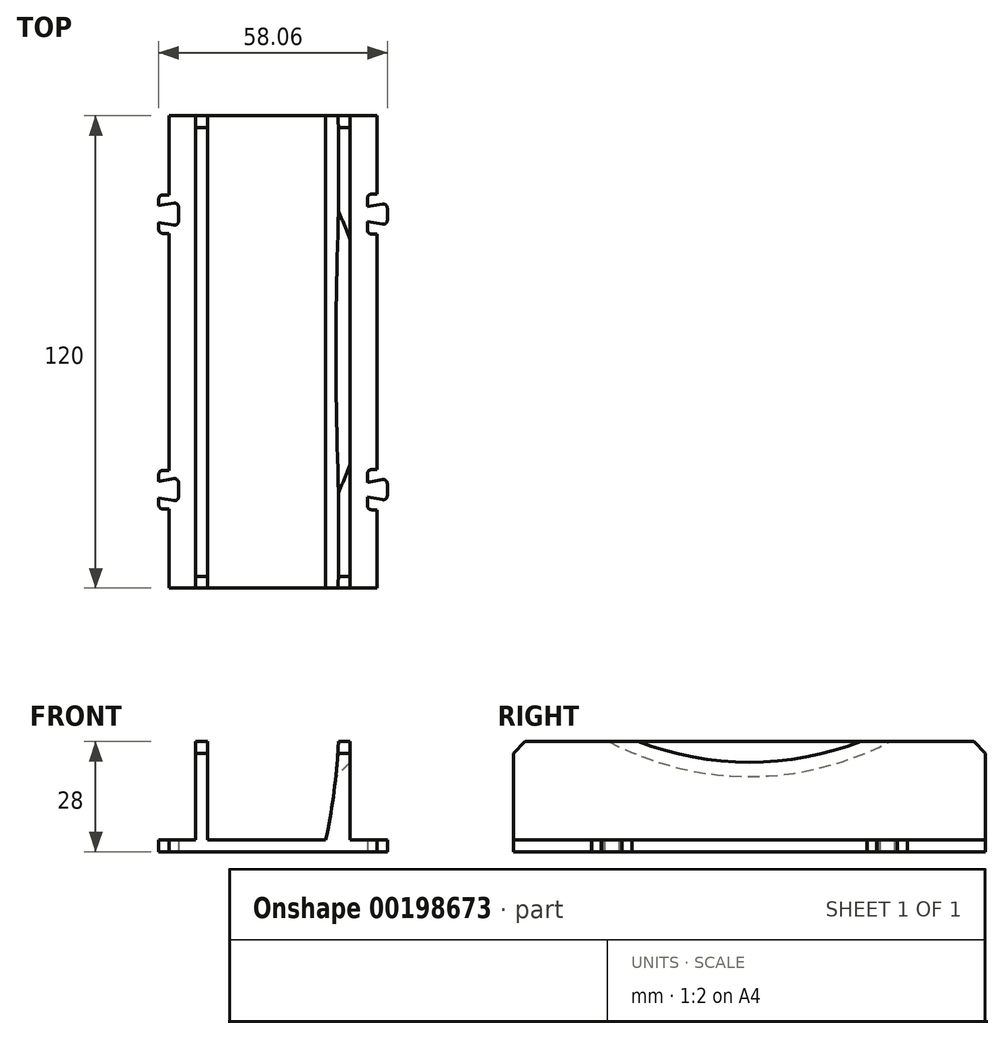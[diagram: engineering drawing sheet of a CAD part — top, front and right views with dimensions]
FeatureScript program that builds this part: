
annotation { "Feature Type Name" : "Feature", "Feature Type Description" : "" }
export const myFeature = defineFeature(function(context is Context, id is Id, definition is map)
    precondition{}
    {
        {
            var Q0;
            Q0=qCreatedBy(makeId("Front.planeOp"),FACE);
            var sketch = newSketch(context, id + "F0", { "sketchPlane" : qUnion([Q0])});
            skLineSegment(sketch, "E0", {"start": v(-26.63, 0) * mm, "end": v(26.63, 0) * mm});
            skLineSegment(sketch, "E1", {"start": v(26.63, 0) * mm, "end": v(26.63, 3) * mm});
            skLineSegment(sketch, "E2", {"start": v(26.63, 3) * mm, "end": v(19.62, 3) * mm});
            skLineSegment(sketch, "E3", {"start": v(19.62, 3) * mm, "end": v(19.62, 28) * mm});
            skLineSegment(sketch, "E4", {"start": v(19.63, 28) * mm, "end": v(16.62, 28) * mm});
            skLineSegment(sketch, "E5", {"start": v(13.38, 3) * mm, "end": v(-16.63, 3) * mm});
            skLineSegment(sketch, "E6", {"start": v(-16.63, 3) * mm, "end": v(-16.62, 28) * mm});
            skLineSegment(sketch, "E7", {"start": v(-16.62, 28) * mm, "end": v(-19.63, 28) * mm});
            skLineSegment(sketch, "E8", {"start": v(-19.63, 28) * mm, "end": v(-19.63, 3) * mm});
            skLineSegment(sketch, "E9", {"start": v(-19.63, 3) * mm, "end": v(-26.63, 3) * mm});
            skLineSegment(sketch, "E10", {"start": v(-26.63, 3) * mm, "end": v(-26.63, 0) * mm});
            skPoint(sketch, "E11", {"position": v(0, 0) * mm});
            skArc(sketch, "E12", {"start": v(16.63, 28) * mm, "mid": v(15.53, 15.43) * mm, "end": v(13.38, 3) * mm});
            skLineSegment(sketch, "E13", {"start": v(-16.62, 28) * mm, "end": v(16.62, 28) * mm, "construction": true});
            skPoint(sketch, "E14", {"position": v(0, 28) * mm});
            skSolve(sketch);
        }
        {
            var Q0;
            Q0=makeQuery(id+"F0.imprint","IMPRINT",FACE,{"disambiguationData":[TD([[makeQuery(id+"F0.imprint","IMPRINT",EDGE,{"derivedFrom":sQuery(id+"F0.wireOp",EDGE,"E0")}),1.0]])]});
            extrude(context, id + "F1", {"entities" : qUnion([Q0]), "depth" : 120 * mm, "symmetric" : true});
        }
        {
            var Q0;
            Q0=makeQuery(id+"F1.opExtrude","SWEPT_FACE",FACE,{"disambiguationData":[OSD([sQuery(id+"F0.wireOp",EDGE,"E3")])]});
            var sketch = newSketch(context, id + "F2", { "sketchPlane" : qUnion([Q0])});
            skCircle(sketch, "E15", {"center": v(0, 101.5) * mm, "radius": 78.75 * mm});
            skSolve(sketch);
        }
        {
            var Q0;
            {var subQ0=sQuery(id+"F2.wireOp",EDGE,"E15");var subQ1=makeQuery(id+"F1.opExtrude","SWEPT_EDGE",EDGE,{"disambiguationData":[OSD([sQuery(id+"F0.wireOp",EDGE,"E3"),sQuery(id+"F0.wireOp",EDGE,"E4")])]});var subQ2=makeQuery(id+"F2.imprint","INTERSECT",VERTEX,{"disambiguationData":[OD(0.0)],"derivedFrom":[subQ1,subQ0]});Q0=makeQuery(id+"F2.imprint","IMPRINT",FACE,{"disambiguationData":[TD([[makeQuery(id+"F2.imprint","IMPRINT",EDGE,{"disambiguationData":[TD([[subQ2,1.0]])],"derivedFrom":subQ0}),1.0]])]});}
            var Q1;
            Q1=makeQuery(id+"F1.opExtrude","SWEPT_FACE",FACE,{"disambiguationData":[OSD([sQuery(id+"F0.wireOp",EDGE,"E12")])]});
            var Q2;
            Q2=makeQuery(id+"F1.opExtrude","SWEPT_BODY",BODY,{"disambiguationData":[OSD([sQuery(id+"F0.wireOp",EDGE,"E0"),sQuery(id+"F0.wireOp",EDGE,"E1"),sQuery(id+"F0.wireOp",EDGE,"E2"),sQuery(id+"F0.wireOp",EDGE,"E3"),sQuery(id+"F0.wireOp",EDGE,"E4"),sQuery(id+"F0.wireOp",EDGE,"E5"),sQuery(id+"F0.wireOp",EDGE,"E6"),sQuery(id+"F0.wireOp",EDGE,"E7"),sQuery(id+"F0.wireOp",EDGE,"E8"),sQuery(id+"F0.wireOp",EDGE,"E9"),sQuery(id+"F0.wireOp",EDGE,"E10"),sQuery(id+"F0.wireOp",EDGE,"E12")])]});
            extrude(context, id + "F3", {"entities" : qUnion([Q0]), "operationType" : NewBodyOperationType.REMOVE, "endBound" : BoundingType.UP_TO_SURFACE, "oppositeDirection" : true, "endBoundEntityFace" : qUnion([Q1]), "endBoundEntityBody" : qUnion([Q2]), "depth" : 25 * mm, "hasDraft" : true, "draftAngle" : 45 * degree});
        }
        {
            var Q0;
            Q0=makeQuery(id+"F1.opExtrude","SWEPT_FACE",FACE,{"disambiguationData":[OSD([sQuery(id+"F0.wireOp",EDGE,"E0")])]});
            var sketch = newSketch(context, id + "F4", { "sketchPlane" : qUnion([Q0])});
            skLineSegment(sketch, "E16.bottom", {"start": v(31.63, 30) * mm, "end": v(24.13, 30) * mm, "construction": true});
            skLineSegment(sketch, "E16.top", {"start": v(31.63, 40) * mm, "end": v(24.13, 40) * mm, "construction": true});
            skLineSegment(sketch, "E16.left", {"start": v(31.63, 30) * mm, "end": v(31.63, 30) * mm});
            skLineSegment(sketch, "E16.right", {"start": v(21.63, 30) * mm, "end": v(21.63, 40) * mm, "construction": true});
            skPoint(sketch, "E16.middle", {"position": v(26.63, 35) * mm});
            skLineSegment(sketch, "E17", {"start": v(24.13, 40) * mm, "end": v(24.13, 37) * mm, "construction": true});
            skLineSegment(sketch, "E18", {"start": v(24.13, 37) * mm, "end": v(29.13, 37.88) * mm, "construction": true});
            skLineSegment(sketch, "E19", {"start": v(29.13, 37.88) * mm, "end": v(29.13, 32.12) * mm, "construction": true});
            skLineSegment(sketch, "E20", {"start": v(29.13, 32.12) * mm, "end": v(24.13, 33) * mm, "construction": true});
            skLineSegment(sketch, "E21", {"start": v(24.13, 33) * mm, "end": v(24.13, 30) * mm, "construction": true});
            skPoint(sketch, "E22", {"position": v(29.13, 35) * mm});
            skLineSegment(sketch, "E23.0.1.2", {"start": v(29.25, -30) * mm, "end": v(29.25, -30) * mm});
            skLineSegment(sketch, "E24", {"start": v(29.25, -20) * mm, "end": v(29.25, -20) * mm});
            skLineSegment(sketch, "E25", {"start": v(24.13, 30) * mm, "end": v(21.63, 30) * mm, "construction": true});
            skLineSegment(sketch, "E26", {"start": v(31.63, 30) * mm, "end": v(31.63, 40) * mm, "construction": true});
            skLineSegment(sketch, "E27", {"start": v(24.13, 40) * mm, "end": v(21.63, 40) * mm, "construction": true});
            skLineSegment(sketch, "E28", {"start": v(31.63, 40) * mm, "end": v(31.63, 40) * mm});
            skLineSegment(sketch, "E29.0.1.0", {"start": v(31.63, -40) * mm, "end": v(24.13, -40) * mm, "construction": true});
            skLineSegment(sketch, "E29.0.1.1", {"start": v(21.63, -40) * mm, "end": v(21.63, -30) * mm, "construction": true});
            skLineSegment(sketch, "E29.0.1.2", {"start": v(24.13, -40) * mm, "end": v(21.63, -40) * mm, "construction": true});
            skLineSegment(sketch, "E29.0.1.3", {"start": v(29.13, -37.88) * mm, "end": v(24.13, -37) * mm, "construction": true});
            skLineSegment(sketch, "E29.0.1.4", {"start": v(31.63, -30) * mm, "end": v(24.13, -30) * mm, "construction": true});
            skLineSegment(sketch, "E29.0.1.5", {"start": v(24.13, -30) * mm, "end": v(24.13, -33) * mm, "construction": true});
            skLineSegment(sketch, "E29.0.1.6", {"start": v(24.13, -33) * mm, "end": v(29.13, -32.12) * mm, "construction": true});
            skLineSegment(sketch, "E29.0.1.7", {"start": v(31.63, -40) * mm, "end": v(31.63, -30) * mm, "construction": true});
            skLineSegment(sketch, "E29.0.1.8", {"start": v(24.13, -37) * mm, "end": v(24.13, -40) * mm, "construction": true});
            skPoint(sketch, "E29.0.1.9", {"position": v(26.63, -35) * mm});
            skPoint(sketch, "E29.0.1.10", {"position": v(29.13, -35) * mm});
            skLineSegment(sketch, "E29.0.1.11", {"start": v(24.13, -30) * mm, "end": v(21.62, -30) * mm, "construction": true});
            skLineSegment(sketch, "E29.0.1.12", {"start": v(29.13, -32.12) * mm, "end": v(29.13, -37.88) * mm, "construction": true});
            skLineSegment(sketch, "E29.1.0.0", {"start": v(-21.63, 30) * mm, "end": v(-29.12, 30) * mm, "construction": true});
            skLineSegment(sketch, "E29.1.0.1", {"start": v(-31.62, 30) * mm, "end": v(-31.62, 40) * mm, "construction": true});
            skLineSegment(sketch, "E29.1.0.2", {"start": v(-29.12, 30) * mm, "end": v(-31.63, 30) * mm, "construction": true});
            skLineSegment(sketch, "E29.1.0.3", {"start": v(-24.12, 32.12) * mm, "end": v(-29.12, 33) * mm, "construction": true});
            skLineSegment(sketch, "E29.1.0.4", {"start": v(-21.62, 40) * mm, "end": v(-29.12, 40) * mm, "construction": true});
            skLineSegment(sketch, "E29.1.0.5", {"start": v(-29.12, 40) * mm, "end": v(-29.12, 37) * mm, "construction": true});
            skLineSegment(sketch, "E29.1.0.6", {"start": v(-29.12, 37) * mm, "end": v(-24.12, 37.88) * mm, "construction": true});
            skLineSegment(sketch, "E29.1.0.7", {"start": v(-21.63, 30) * mm, "end": v(-21.63, 40) * mm, "construction": true});
            skLineSegment(sketch, "E29.1.0.8", {"start": v(-29.12, 33) * mm, "end": v(-29.12, 30) * mm, "construction": true});
            skPoint(sketch, "E29.1.0.9", {"position": v(-26.63, 35) * mm});
            skPoint(sketch, "E29.1.0.10", {"position": v(-24.12, 35) * mm});
            skLineSegment(sketch, "E29.1.0.11", {"start": v(-29.12, 40) * mm, "end": v(-31.62, 40) * mm, "construction": true});
            skLineSegment(sketch, "E29.1.0.12", {"start": v(-24.12, 37.88) * mm, "end": v(-24.12, 32.12) * mm, "construction": true});
            skLineSegment(sketch, "E29.1.1.0", {"start": v(-21.62, -40) * mm, "end": v(-29.12, -40) * mm, "construction": true});
            skLineSegment(sketch, "E29.1.1.1", {"start": v(-31.62, -40) * mm, "end": v(-31.62, -30) * mm, "construction": true});
            skLineSegment(sketch, "E29.1.1.2", {"start": v(-29.12, -40) * mm, "end": v(-31.63, -40) * mm, "construction": true});
            skLineSegment(sketch, "E29.1.1.3", {"start": v(-24.12, -37.88) * mm, "end": v(-29.12, -37) * mm, "construction": true});
            skLineSegment(sketch, "E29.1.1.4", {"start": v(-21.63, -30) * mm, "end": v(-29.12, -30) * mm, "construction": true});
            skLineSegment(sketch, "E29.1.1.5", {"start": v(-29.12, -30) * mm, "end": v(-29.12, -33) * mm, "construction": true});
            skLineSegment(sketch, "E29.1.1.6", {"start": v(-29.12, -33) * mm, "end": v(-24.12, -32.12) * mm, "construction": true});
            skLineSegment(sketch, "E29.1.1.7", {"start": v(-21.63, -40) * mm, "end": v(-21.63, -30) * mm, "construction": true});
            skLineSegment(sketch, "E29.1.1.8", {"start": v(-29.12, -37) * mm, "end": v(-29.12, -40) * mm, "construction": true});
            skPoint(sketch, "E29.1.1.9", {"position": v(-26.63, -35) * mm});
            skPoint(sketch, "E29.1.1.10", {"position": v(-24.13, -35) * mm});
            skLineSegment(sketch, "E29.1.1.11", {"start": v(-29.12, -30) * mm, "end": v(-31.63, -30) * mm, "construction": true});
            skLineSegment(sketch, "E29.1.1.12", {"start": v(-24.12, -32.12) * mm, "end": v(-24.12, -37.88) * mm, "construction": true});
            skLineSegment(sketch, "E29.direction1", {"start": v(21.63, 30) * mm, "end": v(-31.63, 30) * mm, "construction": true});
            skLineSegment(sketch, "E29.direction2", {"start": v(21.63, 30) * mm, "end": v(21.63, -40) * mm, "construction": true});
            skLineSegment(sketch, "E30.0", {"start": v(29.03, -37.76) * mm, "end": v(24.03, -36.88) * mm});
            skLineSegment(sketch, "E30.1", {"start": v(29.03, -32.24) * mm, "end": v(29.03, -37.76) * mm});
            skLineSegment(sketch, "E30.2", {"start": v(24.03, -36.88) * mm, "end": v(24.03, -40.1) * mm});
            skLineSegment(sketch, "E30.3", {"start": v(24.03, -33.12) * mm, "end": v(29.03, -32.24) * mm});
            skLineSegment(sketch, "E30.4", {"start": v(31.73, -40.1) * mm, "end": v(24.03, -40.1) * mm});
            skLineSegment(sketch, "E30.5", {"start": v(31.73, -40.1) * mm, "end": v(31.73, -29.9) * mm});
            skLineSegment(sketch, "E30.6", {"start": v(31.73, -29.9) * mm, "end": v(24.03, -29.9) * mm});
            skLineSegment(sketch, "E30.7", {"start": v(24.03, -29.9) * mm, "end": v(24.03, -33.12) * mm});
            skLineSegment(sketch, "E31.0", {"start": v(31.73, 29.9) * mm, "end": v(31.73, 40.1) * mm});
            skLineSegment(sketch, "E31.1", {"start": v(31.73, 40.1) * mm, "end": v(24.03, 40.1) * mm});
            skLineSegment(sketch, "E31.2", {"start": v(31.73, 29.9) * mm, "end": v(24.03, 29.9) * mm});
            skLineSegment(sketch, "E31.3", {"start": v(24.03, 40.1) * mm, "end": v(24.03, 36.88) * mm});
            skLineSegment(sketch, "E31.4", {"start": v(24.03, 33.12) * mm, "end": v(24.03, 29.9) * mm});
            skLineSegment(sketch, "E31.5", {"start": v(29.03, 32.24) * mm, "end": v(24.03, 33.12) * mm});
            skLineSegment(sketch, "E31.6", {"start": v(29.03, 37.76) * mm, "end": v(29.03, 32.24) * mm});
            skLineSegment(sketch, "E31.7", {"start": v(24.03, 36.88) * mm, "end": v(29.03, 37.76) * mm});
            skLineSegment(sketch, "E32.0", {"start": v(-29.02, 32.88) * mm, "end": v(-29.02, 29.9) * mm});
            skLineSegment(sketch, "E32.1", {"start": v(-24.02, 32) * mm, "end": v(-29.02, 32.88) * mm});
            skLineSegment(sketch, "E32.2", {"start": v(-29.02, 29.9) * mm, "end": v(-31.73, 29.9) * mm});
            skLineSegment(sketch, "E32.3", {"start": v(-24.02, 38) * mm, "end": v(-24.02, 32) * mm});
            skLineSegment(sketch, "E32.4", {"start": v(-31.73, 29.9) * mm, "end": v(-31.73, 40.1) * mm});
            skLineSegment(sketch, "E32.5", {"start": v(-29.02, 40.1) * mm, "end": v(-31.73, 40.1) * mm});
            skLineSegment(sketch, "E32.6", {"start": v(-29.02, 40.1) * mm, "end": v(-29.02, 37.12) * mm});
            skLineSegment(sketch, "E32.7", {"start": v(-29.02, 37.12) * mm, "end": v(-24.02, 38) * mm});
            skLineSegment(sketch, "E33.0", {"start": v(-29.02, -29.9) * mm, "end": v(-29.02, -32.88) * mm});
            skLineSegment(sketch, "E33.1", {"start": v(-29.02, -29.9) * mm, "end": v(-31.73, -29.9) * mm});
            skLineSegment(sketch, "E33.2", {"start": v(-29.02, -32.88) * mm, "end": v(-24.02, -32) * mm});
            skLineSegment(sketch, "E33.3", {"start": v(-31.73, -40.1) * mm, "end": v(-31.73, -29.9) * mm});
            skLineSegment(sketch, "E33.4", {"start": v(-24.02, -32) * mm, "end": v(-24.02, -38) * mm});
            skLineSegment(sketch, "E33.5", {"start": v(-24.02, -38) * mm, "end": v(-29.02, -37.12) * mm});
            skLineSegment(sketch, "E33.6", {"start": v(-29.02, -37.12) * mm, "end": v(-29.02, -40.1) * mm});
            skLineSegment(sketch, "E33.7", {"start": v(-29.02, -40.1) * mm, "end": v(-31.73, -40.1) * mm});
            skLineSegment(sketch, "E34.0", {"start": v(-21.72, -30.1) * mm, "end": v(-29.02, -30.1) * mm});
            skLineSegment(sketch, "E34.1", {"start": v(-21.72, -39.9) * mm, "end": v(-21.72, -30.1) * mm});
            skLineSegment(sketch, "E34.2", {"start": v(-21.72, -39.9) * mm, "end": v(-29.02, -39.9) * mm});
            skLineSegment(sketch, "E35.0", {"start": v(-21.72, 39.9) * mm, "end": v(-29.02, 39.9) * mm});
            skLineSegment(sketch, "E35.1", {"start": v(-21.72, 30.1) * mm, "end": v(-21.72, 39.9) * mm});
            skLineSegment(sketch, "E35.2", {"start": v(-21.72, 30.1) * mm, "end": v(-29.02, 30.1) * mm});
            skSolve(sketch);
        }
        {
            var Q0;
            {var subQ0=sQuery(id+"F4.wireOp",EDGE,"E30.7");Q0=makeQuery(id+"F4.imprint","IMPRINT",FACE,{"disambiguationData":[TD([[makeQuery(id+"F4.imprint","IMPRINT",EDGE,{"derivedFrom":subQ0}),1.0]])]});}
            var Q1;
            {var subQ0=sQuery(id+"F4.wireOp",EDGE,"E30.2");Q1=makeQuery(id+"F4.imprint","IMPRINT",FACE,{"disambiguationData":[TD([[makeQuery(id+"F4.imprint","IMPRINT",EDGE,{"derivedFrom":subQ0}),1.0]])]});}
            var Q2;
            {var subQ0=sQuery(id+"F4.wireOp",EDGE,"E31.4");Q2=makeQuery(id+"F4.imprint","IMPRINT",FACE,{"disambiguationData":[TD([[makeQuery(id+"F4.imprint","IMPRINT",EDGE,{"derivedFrom":subQ0}),1.0]])]});}
            var Q3;
            {var subQ0=sQuery(id+"F4.wireOp",EDGE,"E31.3");Q3=makeQuery(id+"F4.imprint","IMPRINT",FACE,{"disambiguationData":[TD([[makeQuery(id+"F4.imprint","IMPRINT",EDGE,{"derivedFrom":subQ0}),1.0]])]});}
            var Q4;
            {var subQ0=sQuery(id+"F4.wireOp",EDGE,"E32.3");Q4=makeQuery(id+"F4.imprint","IMPRINT",FACE,{"disambiguationData":[TD([[makeQuery(id+"F4.imprint","IMPRINT",EDGE,{"derivedFrom":subQ0}),-1.0]])]});}
            var Q5;
            {var subQ0=sQuery(id+"F4.wireOp",EDGE,"E33.4");Q5=makeQuery(id+"F4.imprint","IMPRINT",FACE,{"disambiguationData":[TD([[makeQuery(id+"F4.imprint","IMPRINT",EDGE,{"derivedFrom":subQ0}),-1.0]])]});}
            extrude(context, id + "F5", {"entities" : qUnion([Q0, Q1, Q2, Q3, Q4, Q5]), "operationType" : NewBodyOperationType.REMOVE, "oppositeDirection" : true, "depth" : 25 * mm, "symmetric" : true});
        }
        {
            var Q0;
            {var subQ0=sQuery(id+"F4.wireOp",EDGE,"E31.6");Q0=makeQuery(id+"F4.imprint","IMPRINT",FACE,{"disambiguationData":[TD([[makeQuery(id+"F4.imprint","IMPRINT",EDGE,{"derivedFrom":subQ0}),-1.0]])]});}
            var Q1;
            {var subQ0=sQuery(id+"F4.wireOp",EDGE,"E30.1");Q1=makeQuery(id+"F4.imprint","IMPRINT",FACE,{"disambiguationData":[TD([[makeQuery(id+"F4.imprint","IMPRINT",EDGE,{"derivedFrom":subQ0}),-1.0]])]});}
            var Q2;
            {var subQ0=sQuery(id+"F4.wireOp",EDGE,"E33.2");var subQ1=sQuery(id+"F4.wireOp",EDGE,"E33.0");var subQ2=makeQuery(id+"F4.imprint","INTERSECT",VERTEX,{"derivedFrom":[subQ1,subQ0]});Q2=makeQuery(id+"F4.imprint","IMPRINT",FACE,{"disambiguationData":[TD([[makeQuery(id+"F4.imprint","IMPRINT",EDGE,{"disambiguationData":[TD([[subQ2,1.0]])],"derivedFrom":subQ1}),1.0]])]});}
            var Q3;
            {var subQ0=sQuery(id+"F4.wireOp",EDGE,"E33.6");var subQ1=sQuery(id+"F4.wireOp",EDGE,"E33.5");var subQ2=makeQuery(id+"F4.imprint","INTERSECT",VERTEX,{"derivedFrom":[subQ1,subQ0]});Q3=makeQuery(id+"F4.imprint","IMPRINT",FACE,{"disambiguationData":[TD([[makeQuery(id+"F4.imprint","IMPRINT",EDGE,{"disambiguationData":[TD([[subQ2,-1.0]])],"derivedFrom":subQ0}),1.0]])]});}
            var Q4;
            {var subQ0=sQuery(id+"F4.wireOp",EDGE,"E32.7");var subQ1=sQuery(id+"F4.wireOp",EDGE,"E32.6");var subQ2=makeQuery(id+"F4.imprint","INTERSECT",VERTEX,{"derivedFrom":[subQ1,subQ0]});Q4=makeQuery(id+"F4.imprint","IMPRINT",FACE,{"disambiguationData":[TD([[makeQuery(id+"F4.imprint","IMPRINT",EDGE,{"disambiguationData":[TD([[subQ2,1.0]])],"derivedFrom":subQ1}),1.0]])]});}
            var Q5;
            {var subQ0=sQuery(id+"F4.wireOp",EDGE,"E32.1");var subQ1=sQuery(id+"F4.wireOp",EDGE,"E32.0");var subQ2=makeQuery(id+"F4.imprint","INTERSECT",VERTEX,{"derivedFrom":[subQ1,subQ0]});Q5=makeQuery(id+"F4.imprint","IMPRINT",FACE,{"disambiguationData":[TD([[makeQuery(id+"F4.imprint","IMPRINT",EDGE,{"disambiguationData":[TD([[subQ2,-1.0]])],"derivedFrom":subQ1}),1.0]])]});}
            var Q6;
            Q6=makeQuery(id+"F1.opExtrude","SWEPT_FACE",FACE,{"disambiguationData":[OSD([sQuery(id+"F0.wireOp",EDGE,"E9")])]});
            extrude(context, id + "F6", {"entities" : qUnion([Q0, Q1, Q2, Q3, Q4, Q5]), "operationType" : NewBodyOperationType.ADD, "endBound" : BoundingType.UP_TO_SURFACE, "oppositeDirection" : true, "endBoundEntityFace" : qUnion([Q6]), "depth" : 25 * mm});
        }
        {
            var Q0;
            Q0=makeQuery(id+"F6.opExtrude","SWEPT_EDGE",EDGE,{"disambiguationData":[OSD([sQuery(id+"F4.wireOp",EDGE,"E32.6"),sQuery(id+"F4.wireOp",EDGE,"E35.0")])]});
            var Q1;
            Q1=makeQuery(id+"F5.boolean.opBoolean","COPY",EDGE,{"derivedFrom":makeQuery(id+"F5.opExtrude","SWEPT_EDGE",EDGE,{"disambiguationData":[OSD([sQuery(id+"F4.wireOp",EDGE,"E32.1"),sQuery(id+"F4.wireOp",EDGE,"E32.3")])]})});
            var Q2;
            Q2=makeQuery(id+"F5.boolean.opBoolean","COPY",EDGE,{"derivedFrom":makeQuery(id+"F5.opExtrude","SWEPT_EDGE",EDGE,{"disambiguationData":[OSD([sQuery(id+"F4.wireOp",EDGE,"E32.3"),sQuery(id+"F4.wireOp",EDGE,"E32.7")])]})});
            var Q3;
            Q3=makeQuery(id+"F6.opExtrude","SWEPT_EDGE",EDGE,{"disambiguationData":[OSD([sQuery(id+"F4.wireOp",EDGE,"E32.0"),sQuery(id+"F4.wireOp",EDGE,"E35.2")])]});
            var Q4;
            Q4=makeQuery(id+"F6.opExtrude","SWEPT_EDGE",EDGE,{"disambiguationData":[OSD([sQuery(id+"F4.wireOp",EDGE,"E33.6"),sQuery(id+"F4.wireOp",EDGE,"E34.2")])]});
            var Q5;
            Q5=makeQuery(id+"F5.boolean.opBoolean","COPY",EDGE,{"derivedFrom":makeQuery(id+"F5.opExtrude","SWEPT_EDGE",EDGE,{"disambiguationData":[OSD([sQuery(id+"F4.wireOp",EDGE,"E33.2"),sQuery(id+"F4.wireOp",EDGE,"E33.4")])]})});
            var Q6;
            Q6=makeQuery(id+"F6.opExtrude","SWEPT_EDGE",EDGE,{"disambiguationData":[OSD([sQuery(id+"F4.wireOp",EDGE,"E33.0"),sQuery(id+"F4.wireOp",EDGE,"E34.0")])]});
            var Q7;
            Q7=makeQuery(id+"F5.boolean.opBoolean","COPY",EDGE,{"derivedFrom":makeQuery(id+"F5.opExtrude","SWEPT_EDGE",EDGE,{"disambiguationData":[OSD([sQuery(id+"F4.wireOp",EDGE,"E33.4"),sQuery(id+"F4.wireOp",EDGE,"E33.5")])]})});
            var Q8;
            Q8=makeQuery(id+"F5.boolean.opBoolean","COPY",EDGE,{"derivedFrom":makeQuery(id+"F5.opExtrude","SWEPT_EDGE",EDGE,{"disambiguationData":[OSD([sQuery(id+"F4.wireOp",EDGE,"E30.2"),sQuery(id+"F4.wireOp",EDGE,"E30.4")])]})});
            var Q9;
            Q9=makeQuery(id+"F6.opExtrude","SWEPT_EDGE",EDGE,{"disambiguationData":[OSD([sQuery(id+"F4.wireOp",EDGE,"E30.1"),sQuery(id+"F4.wireOp",EDGE,"E30.3")])]});
            var Q10;
            Q10=makeQuery(id+"F6.opExtrude","SWEPT_EDGE",EDGE,{"disambiguationData":[OSD([sQuery(id+"F4.wireOp",EDGE,"E30.0"),sQuery(id+"F4.wireOp",EDGE,"E30.1")])]});
            var Q11;
            Q11=makeQuery(id+"F5.boolean.opBoolean","COPY",EDGE,{"derivedFrom":makeQuery(id+"F5.opExtrude","SWEPT_EDGE",EDGE,{"disambiguationData":[OSD([sQuery(id+"F4.wireOp",EDGE,"E30.6"),sQuery(id+"F4.wireOp",EDGE,"E30.7")])]})});
            var Q12;
            Q12=makeQuery(id+"F5.boolean.opBoolean","COPY",EDGE,{"derivedFrom":makeQuery(id+"F5.opExtrude","SWEPT_EDGE",EDGE,{"disambiguationData":[OSD([sQuery(id+"F4.wireOp",EDGE,"E31.1"),sQuery(id+"F4.wireOp",EDGE,"E31.3")])]})});
            var Q13;
            Q13=makeQuery(id+"F6.opExtrude","SWEPT_EDGE",EDGE,{"disambiguationData":[OSD([sQuery(id+"F4.wireOp",EDGE,"E31.5"),sQuery(id+"F4.wireOp",EDGE,"E31.6")])]});
            var Q14;
            Q14=makeQuery(id+"F6.opExtrude","SWEPT_EDGE",EDGE,{"disambiguationData":[OSD([sQuery(id+"F4.wireOp",EDGE,"E31.6"),sQuery(id+"F4.wireOp",EDGE,"E31.7")])]});
            var Q15;
            Q15=makeQuery(id+"F5.boolean.opBoolean","COPY",EDGE,{"derivedFrom":makeQuery(id+"F5.opExtrude","SWEPT_EDGE",EDGE,{"disambiguationData":[OSD([sQuery(id+"F4.wireOp",EDGE,"E31.2"),sQuery(id+"F4.wireOp",EDGE,"E31.4")])]})});
            fillet(context, id + "F7", {"entities" : qUnion([Q0, Q1, Q2, Q3, Q4, Q5, Q6, Q7, Q8, Q9, Q10, Q11, Q12, Q13, Q14, Q15]), "radius" : 1 * mm, "tangentPropagation" : true, "allowEdgeOverflow" : false});
        }
        {
            var Q0;
            Q0=makeQuery(id+"F5.boolean.opBoolean","SPLIT",FACE,{"disambiguationData":[TD([makeQuery(id+"F5.opExtrude","SWEPT_FACE",FACE,{"disambiguationData":[OSD([sQuery(id+"F4.wireOp",EDGE,"E30.6")])]})])],"derivedFrom":makeQuery(id+"F1.opExtrude","SWEPT_FACE",FACE,{"disambiguationData":[OSD([sQuery(id+"F0.wireOp",EDGE,"E1")])]})});
            var Q1;
            {var subQ2=sQuery(id+"F0.wireOp",EDGE,"E1");Q1=makeQuery(id+"F5.boolean.opBoolean","SPLIT",FACE,{"disambiguationData":[TD([makeQuery(id+"F5.opExtrude","SWEPT_FACE",FACE,{"disambiguationData":[OSD([sQuery(id+"F4.wireOp",EDGE,"E31.1")])]})])],"derivedFrom":makeQuery(id+"F1.opExtrude","SWEPT_FACE",FACE,{"disambiguationData":[OSD([subQ2])]})});}
            var Q2;
            {var subQ2=sQuery(id+"F0.wireOp",EDGE,"E1");Q2=makeQuery(id+"F5.boolean.opBoolean","SPLIT",FACE,{"disambiguationData":[TD([makeQuery(id+"F5.opExtrude","SWEPT_FACE",FACE,{"disambiguationData":[OSD([sQuery(id+"F4.wireOp",EDGE,"E30.4")])]})])],"derivedFrom":makeQuery(id+"F1.opExtrude","SWEPT_FACE",FACE,{"disambiguationData":[OSD([subQ2])]})});}
            extrude(context, id + "F8", {"entities" : qUnion([Q0, Q1, Q2]), "operationType" : NewBodyOperationType.REMOVE, "oppositeDirection" : true, "depth" : 0.15 * mm});
        }
        {
            var Q0;
            {var subQ1=sQuery(id+"F0.wireOp",EDGE,"E10");Q0=makeQuery(id+"F5.boolean.opBoolean","SPLIT",FACE,{"disambiguationData":[TD([makeQuery(id+"F5.opExtrude","SWEPT_FACE",FACE,{"disambiguationData":[OSD([sQuery(id+"F4.wireOp",EDGE,"E32.7")])]})])],"derivedFrom":makeQuery(id+"F1.opExtrude","SWEPT_FACE",FACE,{"disambiguationData":[OSD([subQ1])]})});}
            var Q1;
            Q1=makeQuery(id+"F5.boolean.opBoolean","SPLIT",FACE,{"disambiguationData":[TD([makeQuery(id+"F5.opExtrude","SWEPT_FACE",FACE,{"disambiguationData":[OSD([sQuery(id+"F4.wireOp",EDGE,"E32.1")])]})])],"derivedFrom":makeQuery(id+"F1.opExtrude","SWEPT_FACE",FACE,{"disambiguationData":[OSD([sQuery(id+"F0.wireOp",EDGE,"E10")])]})});
            var Q2;
            {var subQ1=sQuery(id+"F0.wireOp",EDGE,"E10");Q2=makeQuery(id+"F5.boolean.opBoolean","SPLIT",FACE,{"disambiguationData":[TD([makeQuery(id+"F5.opExtrude","SWEPT_FACE",FACE,{"disambiguationData":[OSD([sQuery(id+"F4.wireOp",EDGE,"E33.5")])]})])],"derivedFrom":makeQuery(id+"F1.opExtrude","SWEPT_FACE",FACE,{"disambiguationData":[OSD([subQ1])]})});}
            extrude(context, id + "F9", {"entities" : qUnion([Q0, Q1, Q2]), "operationType" : NewBodyOperationType.REMOVE, "oppositeDirection" : true, "depth" : 0.15 * mm});
        }
        {
            var Q0;
            Q0=makeQuery(id+"F1.opExtrude","CAP_EDGE",EDGE,{"disambiguationData":[OSD([sQuery(id+"F0.wireOp",EDGE,"E7")])],"isStart":false});
            var Q1;
            Q1=makeQuery(id+"F1.opExtrude","CAP_EDGE",EDGE,{"disambiguationData":[OSD([sQuery(id+"F0.wireOp",EDGE,"E4")])],"isStart":false});
            var Q2;
            Q2=makeQuery(id+"F1.opExtrude","CAP_EDGE",EDGE,{"disambiguationData":[OSD([sQuery(id+"F0.wireOp",EDGE,"E4")])],"isStart":true});
            var Q3;
            Q3=makeQuery(id+"F1.opExtrude","CAP_EDGE",EDGE,{"disambiguationData":[OSD([sQuery(id+"F0.wireOp",EDGE,"E7")])],"isStart":true});
            var Q4;
            {var subQ0=sQuery(id+"F0.wireOp",EDGE,"E1");Q4=makeQuery(id+"F8.boolean.opBoolean","COPY",EDGE,{"derivedFrom":makeQuery(id+"F8.opExtrude","CAP_EDGE",EDGE,{"disambiguationData":[OSD([subQ0]),TDD([makeQuery(id+"F1.opExtrude","CAP_EDGE",EDGE,{"disambiguationData":[OSD([subQ0])],"isStart":false})])],"isStart":false})});}
            var Q5;
            {var subQ0=sQuery(id+"F0.wireOp",EDGE,"E10");Q5=makeQuery(id+"F9.boolean.opBoolean","COPY",EDGE,{"derivedFrom":makeQuery(id+"F9.opExtrude","CAP_EDGE",EDGE,{"disambiguationData":[OSD([subQ0]),TDD([makeQuery(id+"F1.opExtrude","CAP_EDGE",EDGE,{"disambiguationData":[OSD([subQ0])],"isStart":false})])],"isStart":false})});}
            var Q6;
            {var subQ0=sQuery(id+"F0.wireOp",EDGE,"E10");Q6=makeQuery(id+"F9.boolean.opBoolean","COPY",EDGE,{"derivedFrom":makeQuery(id+"F9.opExtrude","CAP_EDGE",EDGE,{"disambiguationData":[OSD([subQ0]),TDD([makeQuery(id+"F1.opExtrude","CAP_EDGE",EDGE,{"disambiguationData":[OSD([subQ0])],"isStart":true})])],"isStart":false})});}
            var Q7;
            {var subQ0=sQuery(id+"F0.wireOp",EDGE,"E1");Q7=makeQuery(id+"F8.boolean.opBoolean","COPY",EDGE,{"derivedFrom":makeQuery(id+"F8.opExtrude","CAP_EDGE",EDGE,{"disambiguationData":[OSD([subQ0]),TDD([makeQuery(id+"F1.opExtrude","CAP_EDGE",EDGE,{"disambiguationData":[OSD([subQ0])],"isStart":true})])],"isStart":false})});}
            chamfer(context, id + "F10", {"entities" : qUnion([Q0, Q1, Q2, Q3, Q4, Q5, Q6, Q7]), "width" : 3 * mm, "tangentPropagation" : true});
        }
    });
